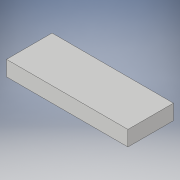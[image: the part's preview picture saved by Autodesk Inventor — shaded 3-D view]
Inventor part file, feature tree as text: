
AUTODESK INVENTOR PART (.ipt)
format: ipt  version: 2019.4 (Build 234330000, 330)  size: 88,064 bytes
history: native  units: in
note: dims shown in document units (in); Inventor stores cm internally (conversion verified against a paired STEP export)
features: extrude x1, sketch x1
ambient origin geometry x8: Origin, YZ Plane, XZ Plane, XY Plane, X Axis, Y Axis, Z Axis, Center Point
bodies: Solid1 (feature_tree)
feature tree (2):
  extrude  "Extrusion1"  Depth=1.1811in
  sketch  "Sketch1"  dims[d0=3.1496in d1=1.1811in d2=0.3937in d3=0.0in]
